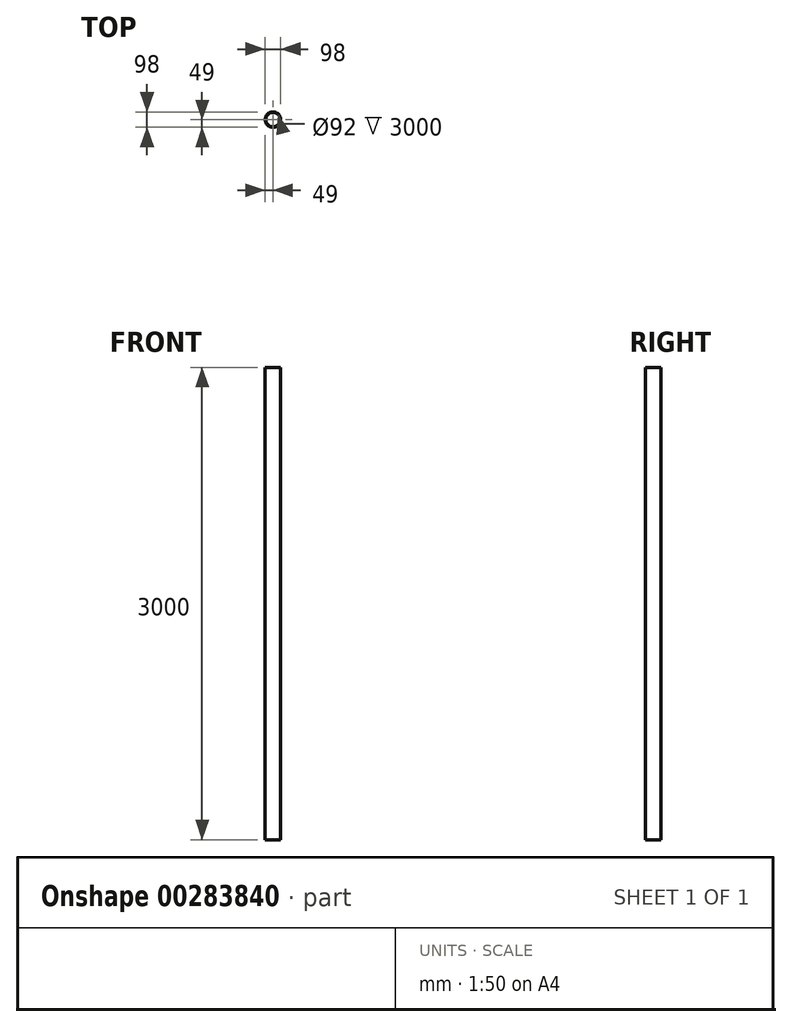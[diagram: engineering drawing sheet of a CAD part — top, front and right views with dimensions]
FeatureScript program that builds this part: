
annotation { "Feature Type Name" : "Feature", "Feature Type Description" : "" }
export const myFeature = defineFeature(function(context is Context, id is Id, definition is map)
    precondition{}
    {
        {
            var Q0;
            Q0=qCreatedBy(makeId("Top.planeOp"),FACE);
            var sketch = newSketch(context, id + "F0", { "sketchPlane" : qUnion([Q0])});
            skCircle(sketch, "E0", {"center": v(0, 0) * mm, "radius": 49 * mm});
            skCircle(sketch, "E1", {"center": v(0, 0) * mm, "radius": 46 * mm});
            skSolve(sketch);
        }
        {
            var Q0;
            Q0 = qSketchRegion(id + "F0", true);
            extrude(context, id + "F1", {"entities" : qUnion([Q0]), "depth" : 3000 * mm});
        }
    });
